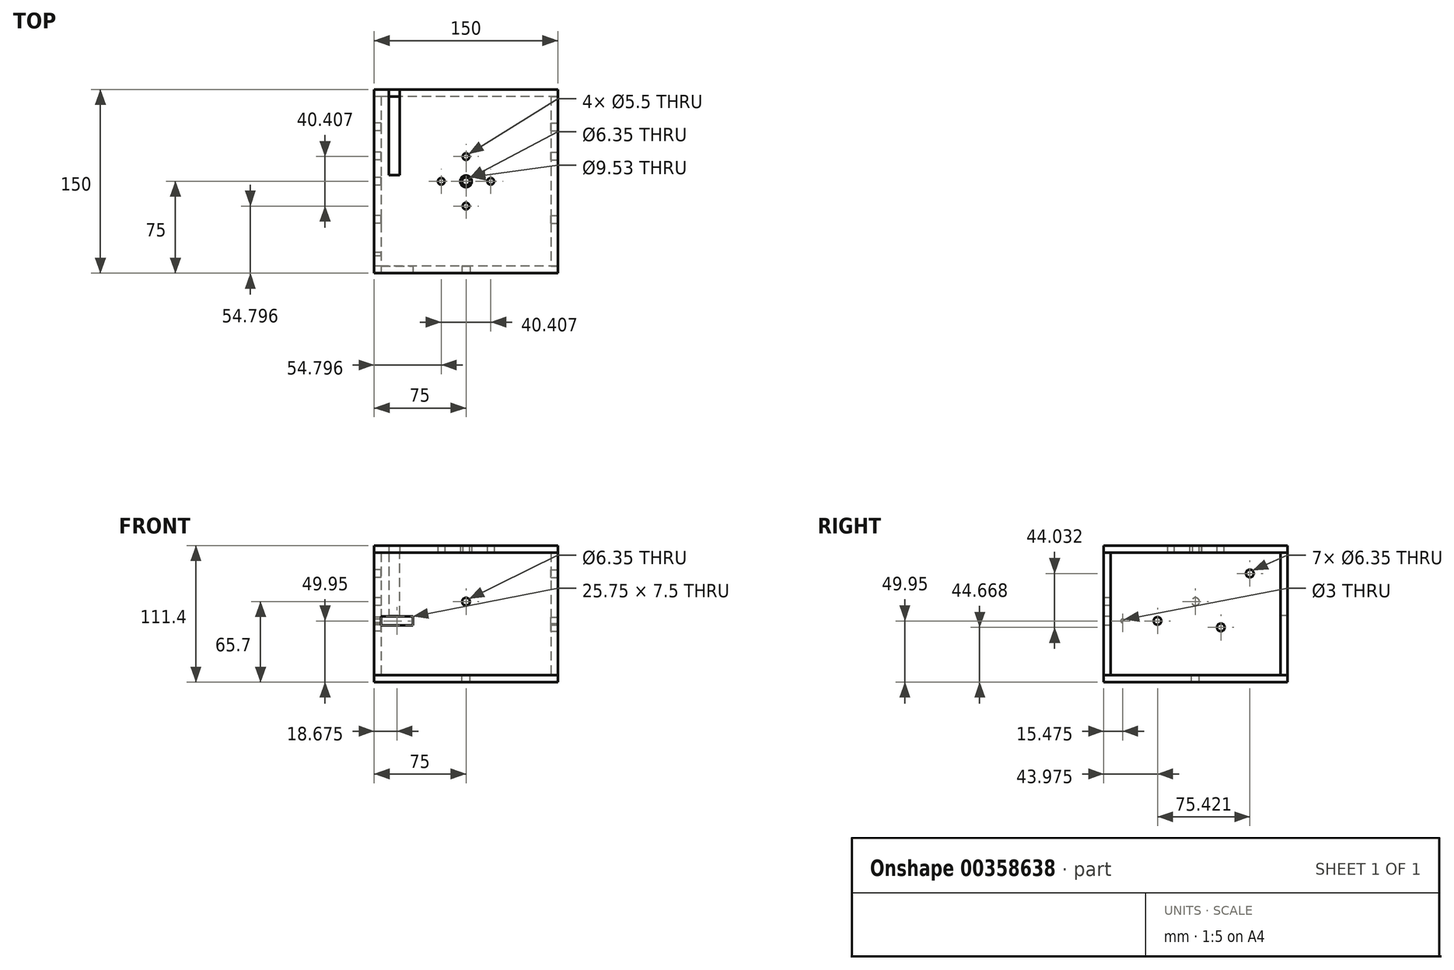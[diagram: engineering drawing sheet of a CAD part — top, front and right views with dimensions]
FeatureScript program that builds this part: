
annotation { "Feature Type Name" : "Feature", "Feature Type Description" : "" }
export const myFeature = defineFeature(function(context is Context, id is Id, definition is map)
    precondition{}
    {
        {
            var Q0;
            Q0=qCreatedBy(makeId("Top.planeOp"),FACE);
            var sketch = newSketch(context, id + "F0", { "sketchPlane" : qUnion([Q0])});
            skLineSegment(sketch, "E0.bottom", {"start": v(75, 75) * mm, "end": v(-54, 75) * mm});
            skLineSegment(sketch, "E0.top", {"start": v(75, -75) * mm, "end": v(-75, -75) * mm});
            skLineSegment(sketch, "E0.left", {"start": v(75, 75) * mm, "end": v(75, -75) * mm});
            skLineSegment(sketch, "E0.right", {"start": v(-75, 75) * mm, "end": v(-75, -75) * mm});
            skPoint(sketch, "E0.middle", {"position": v(0, 0) * mm});
            skCircle(sketch, "E1", {"center": v(0, 0) * mm, "radius": 4.76 * mm});
            skCircle(sketch, "E2", {"center": v(20.2, 0) * mm, "radius": 2.75 * mm});
            skCircle(sketch, "E3.1.0", {"center": v(0, 20.2) * mm, "radius": 2.75 * mm});
            skCircle(sketch, "E3.2.0", {"center": v(-20.2, 0) * mm, "radius": 2.75 * mm});
            skCircle(sketch, "E3.3.0", {"center": v(0, -20.2) * mm, "radius": 2.75 * mm});
            skLineSegment(sketch, "E4", {"start": v(-63, 75) * mm, "end": v(-63, 5) * mm});
            skLineSegment(sketch, "E5", {"start": v(-63, 5) * mm, "end": v(-54, 5) * mm});
            skLineSegment(sketch, "E6", {"start": v(-54, 5) * mm, "end": v(-54, 75) * mm});
            skLineSegment(sketch, "E7.trimOffspring", {"start": v(-63, 75) * mm, "end": v(-75, 75) * mm});
            skSolve(sketch);
        }
        {
            var Q0;
            Q0=makeQuery(id+"F0.imprint","IMPRINT",FACE,{"disambiguationData":[TD([[makeQuery(id+"F0.imprint","IMPRINT",EDGE,{"derivedFrom":sQuery(id+"F0.wireOp",EDGE,"E0.bottom")}),1.0]])]});
            extrude(context, id + "F1", {"entities" : qUnion([Q0]), "depth" : 5.7 * mm, "offsetDistance" : 25 * mm});
        }
        {
            var Q0;
            Q0=makeQuery(id+"F1.opExtrude","SWEPT_FACE",FACE,{"disambiguationData":[OSD([sQuery(id+"F0.wireOp",EDGE,"E0.top")])]});
            var sketch = newSketch(context, id + "F2", { "sketchPlane" : qUnion([Q0])});
            skLineSegment(sketch, "E8.bottom", {"start": v(-75, 0) * mm, "end": v(75, 0) * mm});
            skLineSegment(sketch, "E8.top", {"start": v(-75, -100) * mm, "end": v(75, -100) * mm});
            skLineSegment(sketch, "E8.left", {"start": v(-75, 0) * mm, "end": v(-75, -100) * mm});
            skLineSegment(sketch, "E8.right", {"start": v(75, 0) * mm, "end": v(75, -100) * mm});
            skCircle(sketch, "E9", {"center": v(0, -40) * mm, "radius": 3.17 * mm});
            skLineSegment(sketch, "E10.bottom", {"start": v(-69.2, -52) * mm, "end": v(-43.45, -52) * mm});
            skLineSegment(sketch, "E10.top", {"start": v(-69.2, -59.5) * mm, "end": v(-43.45, -59.5) * mm});
            skLineSegment(sketch, "E10.left", {"start": v(-69.2, -52) * mm, "end": v(-69.2, -59.5) * mm});
            skLineSegment(sketch, "E10.right", {"start": v(-43.45, -52) * mm, "end": v(-43.45, -59.5) * mm});
            skSolve(sketch);
        }
        {
            var Q0;
            Q0 = qSketchRegion(id + "F2", true);
            extrude(context, id + "F3", {"entities" : qUnion([Q0]), "oppositeDirection" : true, "depth" : 5.7 * mm, "offsetDistance" : 25 * mm});
        }
        {
            var Q0;
            Q0=makeQuery(id+"F1.opExtrude","SWEPT_FACE",FACE,{"disambiguationData":[OSD([sQuery(id+"F0.wireOp",EDGE,"E0.left")])]});
            var sketch = newSketch(context, id + "F4", { "sketchPlane" : qUnion([Q0])});
            skLineSegment(sketch, "E11.bottom", {"start": v(-69.3, 0) * mm, "end": v(69.3, 0) * mm});
            skLineSegment(sketch, "E11.top", {"start": v(-69.3, -100) * mm, "end": v(69.3, -100) * mm});
            skLineSegment(sketch, "E11.left", {"start": v(-69.3, 0) * mm, "end": v(-69.3, -100) * mm});
            skLineSegment(sketch, "E11.right", {"start": v(69.3, 0) * mm, "end": v(69.3, -100) * mm});
            skCircle(sketch, "E12", {"center": v(-31.03, -55.75) * mm, "radius": 3.17 * mm});
            skCircle(sketch, "E13", {"center": v(-31.03, -55.75) * mm, "radius": 36 * mm, "construction": true});
            skCircle(sketch, "E14", {"center": v(20.7, -61.03) * mm, "radius": 16 * mm, "construction": true});
            skCircle(sketch, "E15", {"center": v(20.7, -61.03) * mm, "radius": 3.17 * mm});
            skCircle(sketch, "E16", {"center": v(20.7, -61.03) * mm, "radius": 36 * mm, "construction": true});
            skCircle(sketch, "E17", {"center": v(44.4, -17) * mm, "radius": 14 * mm, "construction": true});
            skCircle(sketch, "E18", {"center": v(44.4, -17) * mm, "radius": 36 * mm, "construction": true});
            skCircle(sketch, "E19", {"center": v(44.4, -17) * mm, "radius": 3.17 * mm});
            skCircle(sketch, "E20", {"center": v(0, -40) * mm, "radius": 14 * mm, "construction": true});
            skCircle(sketch, "E21", {"center": v(44.4, -17) * mm, "radius": 16 * mm, "construction": true});
            skCircle(sketch, "E22", {"center": v(20.7, -61.03) * mm, "radius": 38 * mm, "construction": true});
            skSolve(sketch);
        }
        {
            var Q0;
            Q0 = qSketchRegion(id + "F4", true);
            extrude(context, id + "F5", {"entities" : qUnion([Q0]), "oppositeDirection" : true, "depth" : 5.7 * mm, "offsetDistance" : 25 * mm});
        }
        {
            var Q0;
            Q0=makeQuery(id+"F3.opExtrude","SWEPT_FACE",FACE,{"disambiguationData":[OSD([sQuery(id+"F2.wireOp",EDGE,"E8.top")])]});
            var sketch = newSketch(context, id + "F6", { "sketchPlane" : qUnion([Q0])});
            skLineSegment(sketch, "E23.bottom", {"start": v(-75, 75) * mm, "end": v(75, 75) * mm});
            skLineSegment(sketch, "E23.top", {"start": v(-75, -75) * mm, "end": v(75, -75) * mm});
            skLineSegment(sketch, "E23.left", {"start": v(-75, 75) * mm, "end": v(-75, -75) * mm});
            skLineSegment(sketch, "E23.right", {"start": v(75, 75) * mm, "end": v(75, -75) * mm});
            skCircle(sketch, "E24", {"center": v(0, 0) * mm, "radius": 3.17 * mm});
            skSolve(sketch);
        }
        {
            var Q0;
            Q0 = qSketchRegion(id + "F6", true);
            extrude(context, id + "F7", {"entities" : qUnion([Q0]), "depth" : 5.7 * mm, "offsetDistance" : 25 * mm});
        }
        {
            var Q0;
            Q0=makeQuery(id+"F1.opExtrude","SWEPT_FACE",FACE,{"disambiguationData":[OSD([sQuery(id+"F0.wireOp",EDGE,"E0.right")])]});
            var sketch = newSketch(context, id + "F8", { "sketchPlane" : qUnion([Q0])});
            skLineSegment(sketch, "E25.bottom", {"start": v(-69.3, 0) * mm, "end": v(69.3, 0) * mm, "construction": true});
            skLineSegment(sketch, "E25.right", {"start": v(69.3, 0) * mm, "end": v(69.3, -100) * mm, "construction": true});
            skCircle(sketch, "E26", {"center": v(59.52, -55.75) * mm, "radius": 1.5 * mm});
            skCircle(sketch, "E27", {"center": v(0, -40) * mm, "radius": 3.17 * mm});
            skPoint(sketch, "E27.centerSnap0", {"position": v(0, 0) * mm});
            skSolve(sketch);
        }
        {
            var Q0;
            Q0=makeQuery(id+"F5.opExtrude","SWEPT_BODY",BODY,{"disambiguationData":[OSD([sQuery(id+"F4.wireOp",EDGE,"E11.bottom"),sQuery(id+"F4.wireOp",EDGE,"E11.top"),sQuery(id+"F4.wireOp",EDGE,"E11.left"),sQuery(id+"F4.wireOp",EDGE,"E11.right"),sQuery(id+"F4.wireOp",EDGE,"E12"),sQuery(id+"F4.wireOp",EDGE,"E15"),sQuery(id+"F4.wireOp",EDGE,"E19")])]});
            var Q1;
            Q1=qCreatedBy(makeId("Right.planeOp"),FACE);
            mirror(context, id + "F9", {"entities" : qUnion([Q0]), "mirrorPlane" : qUnion([Q1])});
        }
        {
            var Q0;
            Q0=makeQuery(id+"F1.opExtrude","SWEPT_FACE",FACE,{"disambiguationData":[OSD([sQuery(id+"F0.wireOp",EDGE,"E0.bottom")])]});
            var sketch = newSketch(context, id + "F10", { "sketchPlane" : qUnion([Q0])});
            skLineSegment(sketch, "E28.bottom", {"start": v(-75, 0) * mm, "end": v(54, 0) * mm});
            skLineSegment(sketch, "E28.top", {"start": v(-75, -100) * mm, "end": v(75, -100) * mm});
            skLineSegment(sketch, "E28.left", {"start": v(-75, 0) * mm, "end": v(-75, -100) * mm});
            skLineSegment(sketch, "E28.right", {"start": v(75, 0) * mm, "end": v(75, -100) * mm});
            skLineSegment(sketch, "E29", {"start": v(63, 0) * mm, "end": v(63, -51) * mm});
            skLineSegment(sketch, "E30", {"start": v(63, -51) * mm, "end": v(54, -51) * mm});
            skLineSegment(sketch, "E31", {"start": v(54, -51) * mm, "end": v(54, 0) * mm});
            skLineSegment(sketch, "E32.trimOffspring", {"start": v(63, 0) * mm, "end": v(75, 0) * mm});
            skSolve(sketch);
        }
        {
            var Q0;
            Q0 = qSketchRegion(id + "F10", true);
            extrude(context, id + "F11", {"entities" : qUnion([Q0]), "oppositeDirection" : true, "depth" : 5.7 * mm, "offsetDistance" : 25 * mm});
        }
        {
            var Q0;
            Q0 = qSketchRegion(id + "F8", true);
            extrude(context, id + "F12", {"entities" : qUnion([Q0]), "operationType" : NewBodyOperationType.REMOVE, "oppositeDirection" : true, "depth" : 25 * mm, "offsetDistance" : 25 * mm});
        }
    });
